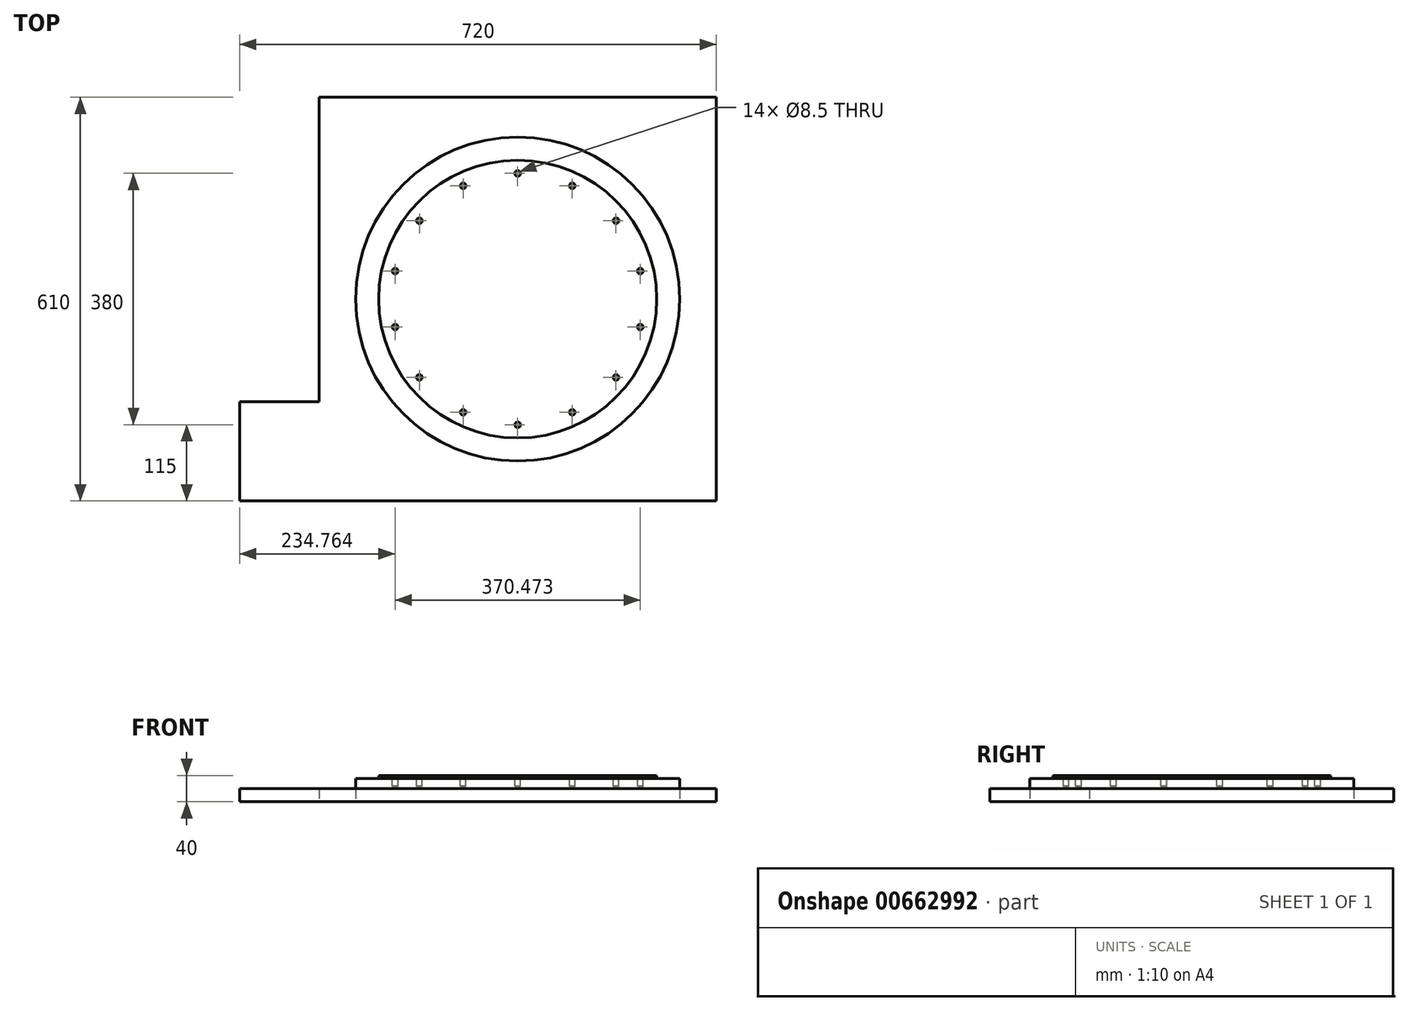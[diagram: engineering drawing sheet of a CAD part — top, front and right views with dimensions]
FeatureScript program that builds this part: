
annotation { "Feature Type Name" : "Feature", "Feature Type Description" : "" }
export const myFeature = defineFeature(function(context is Context, id is Id, definition is map)
    precondition{}
    {
        {
            var Q0;
            Q0=qCreatedBy(makeId("Top.planeOp"),FACE);
            var sketch = newSketch(context, id + "F0", { "sketchPlane" : qUnion([Q0])});
            skLineSegment(sketch, "E0.bottom", {"start": v(300, -305) * mm, "end": v(-300, -305) * mm});
            skLineSegment(sketch, "E0.top", {"start": v(300, 305) * mm, "end": v(-300, 305) * mm});
            skLineSegment(sketch, "E0.left", {"start": v(300, -305) * mm, "end": v(300, 305) * mm});
            skLineSegment(sketch, "E0.right", {"start": v(-300, -155) * mm, "end": v(-300, 305) * mm});
            skPoint(sketch, "E0.middle", {"position": v(0, 0) * mm});
            skLineSegment(sketch, "E1.bottom", {"start": v(-300, -305) * mm, "end": v(-420, -305) * mm});
            skLineSegment(sketch, "E1.top", {"start": v(-300, -155) * mm, "end": v(-420, -155) * mm});
            skLineSegment(sketch, "E1.right", {"start": v(-420, -305) * mm, "end": v(-420, -155) * mm});
            skSolve(sketch);
        }
        {
            var Q0;
            Q0=makeQuery(id+"F0.imprint","IMPRINT",FACE,{"disambiguationData":[TD([[makeQuery(id+"F0.imprint","IMPRINT",EDGE,{"derivedFrom":sQuery(id+"F0.wireOp",EDGE,"E0.bottom")}),-1.0]])]});
            extrude(context, id + "F1", {"entities" : qUnion([Q0]), "depth" : 20 * mm, "offsetDistance" : 25 * mm});
        }
        {
            var Q0;
            Q0=qCreatedBy(makeId("Top.planeOp"),FACE);
            var sketch = newSketch(context, id + "F2", { "sketchPlane" : qUnion([Q0])});
            skCircle(sketch, "E2", {"center": v(0, 0) * mm, "radius": 245 * mm});
            skSolve(sketch);
        }
        {
            var Q0;
            Q0=makeQuery(id+"F2.imprint","IMPRINT",FACE,{"disambiguationData":[TD([[makeQuery(id+"F2.imprint","IMPRINT",EDGE,{"derivedFrom":sQuery(id+"F2.wireOp",EDGE,"E2")}),1.0]])]});
            extrude(context, id + "F3", {"entities" : qUnion([Q0]), "depth" : 35 * mm, "offsetDistance" : 25 * mm});
        }
        {
            var Q0;
            Q0=makeQuery(id+"F3.opExtrude","CAP_FACE",FACE,{"disambiguationData":[OSD([sQuery(id+"F2.wireOp",EDGE,"E2")])],"isStart":false});
            var sketch = newSketch(context, id + "F4", { "sketchPlane" : qUnion([Q0])});
            skCircle(sketch, "E3", {"center": v(0, 0) * mm, "radius": 210 * mm});
            skSolve(sketch);
        }
        {
            var Q0;
            Q0=makeQuery(id+"F4.imprint","IMPRINT",FACE,{"disambiguationData":[TD([[makeQuery(id+"F4.imprint","IMPRINT",EDGE,{"derivedFrom":sQuery(id+"F4.wireOp",EDGE,"E3")}),1.0]])]});
            extrude(context, id + "F5", {"entities" : qUnion([Q0]), "operationType" : NewBodyOperationType.ADD, "depth" : 5 * mm, "offsetDistance" : 25 * mm});
        }
        {
            var Q0;
            Q0=makeQuery(id+"F5.opExtrude","CAP_FACE",FACE,{"disambiguationData":[OSD([sQuery(id+"F4.wireOp",EDGE,"E3")])],"isStart":false});
            var sketch = newSketch(context, id + "F6", { "sketchPlane" : qUnion([Q0])});
            skCircle(sketch, "E4", {"center": v(0, 0) * mm, "radius": 190 * mm, "construction": true});
            skPoint(sketch, "E5", {"position": v(0, 190) * mm});
            skLineSegment(sketch, "E6", {"start": v(0, 0) * mm, "end": v(0, 190) * mm, "construction": true});
            skPoint(sketch, "E7.1.0", {"position": v(-82.44, 171.18) * mm});
            skPoint(sketch, "E7.2.0", {"position": v(-148.55, 118.46) * mm});
            skPoint(sketch, "E7.3.0", {"position": v(-185.24, 42.28) * mm});
            skPoint(sketch, "E7.4.0", {"position": v(-185.24, -42.28) * mm});
            skPoint(sketch, "E7.5.0", {"position": v(-148.55, -118.46) * mm});
            skPoint(sketch, "E7.6.0", {"position": v(-82.44, -171.18) * mm});
            skPoint(sketch, "E7.7.0", {"position": v(0, -190) * mm});
            skPoint(sketch, "E7.8.0", {"position": v(82.44, -171.18) * mm});
            skPoint(sketch, "E7.9.0", {"position": v(148.55, -118.46) * mm});
            skPoint(sketch, "E7.10.0", {"position": v(185.24, -42.28) * mm});
            skPoint(sketch, "E7.11.0", {"position": v(185.24, 42.28) * mm});
            skPoint(sketch, "E7.12.0", {"position": v(148.55, 118.46) * mm});
            skPoint(sketch, "E7.13.0", {"position": v(82.44, 171.18) * mm});
            skSolve(sketch);
        }
        {
            var Q0;
            Q0=sQuery(id+"F6.wireOp",VERTEX,"E5");
            var Q1;
            Q1=sQuery(id+"F6.wireOp",VERTEX,"E7.13.0");
            var Q2;
            Q2=sQuery(id+"F6.wireOp",VERTEX,"E7.12.0");
            var Q3;
            Q3=sQuery(id+"F6.wireOp",VERTEX,"E7.11.0");
            var Q4;
            Q4=sQuery(id+"F6.wireOp",VERTEX,"E7.10.0");
            var Q5;
            Q5=sQuery(id+"F6.wireOp",VERTEX,"E7.9.0");
            var Q6;
            Q6=sQuery(id+"F6.wireOp",VERTEX,"E7.8.0");
            var Q7;
            Q7=sQuery(id+"F6.wireOp",VERTEX,"E7.7.0");
            var Q8;
            Q8=sQuery(id+"F6.wireOp",VERTEX,"E7.6.0");
            var Q9;
            Q9=sQuery(id+"F6.wireOp",VERTEX,"E7.5.0");
            var Q10;
            Q10=sQuery(id+"F6.wireOp",VERTEX,"E7.4.0");
            var Q11;
            Q11=sQuery(id+"F6.wireOp",VERTEX,"E7.3.0");
            var Q12;
            Q12=sQuery(id+"F6.wireOp",VERTEX,"E7.2.0");
            var Q13;
            Q13=sQuery(id+"F6.wireOp",VERTEX,"E7.1.0");
            var Q14;
            Q14=makeQuery(id+"F3.opExtrude","SWEPT_BODY",BODY,{"disambiguationData":[OSD([sQuery(id+"F2.wireOp",EDGE,"E2")])]});
            hole(context, id + "F7", {"style" : HoleStyle.SIMPLE, "endStyle" : HoleEndStyle.BLIND, "standardTappedOrClearance" : lookupTablePath({ "standard" : "ISO", "engagement" : "75%", "pitch" : "1.5 mm", "size" : "M10", "type" : "Tapped" }), "standardBlindInLast" : lookupTablePath({ "standard" : "ISO", "fit" : "Normal", "engagement" : "75%", "pitch" : "1.5 mm", "size" : "M10", "type" : "Clearance & tapped" }), "holeDiameter" : 8.5 * mm, "majorDiameter" : 10 * mm, "showTappedDepth" : true, "holeDepth" : 16.5 * mm, "isTappedThrough" : true, "tappedDepth" : 12 * mm, "tapClearance" : 3, "locations" : qUnion([Q0, Q1, Q2, Q3, Q4, Q5, Q6, Q7, Q8, Q9, Q10, Q11, Q12, Q13]), "scope" : qUnion([Q14])});
        }
    });
